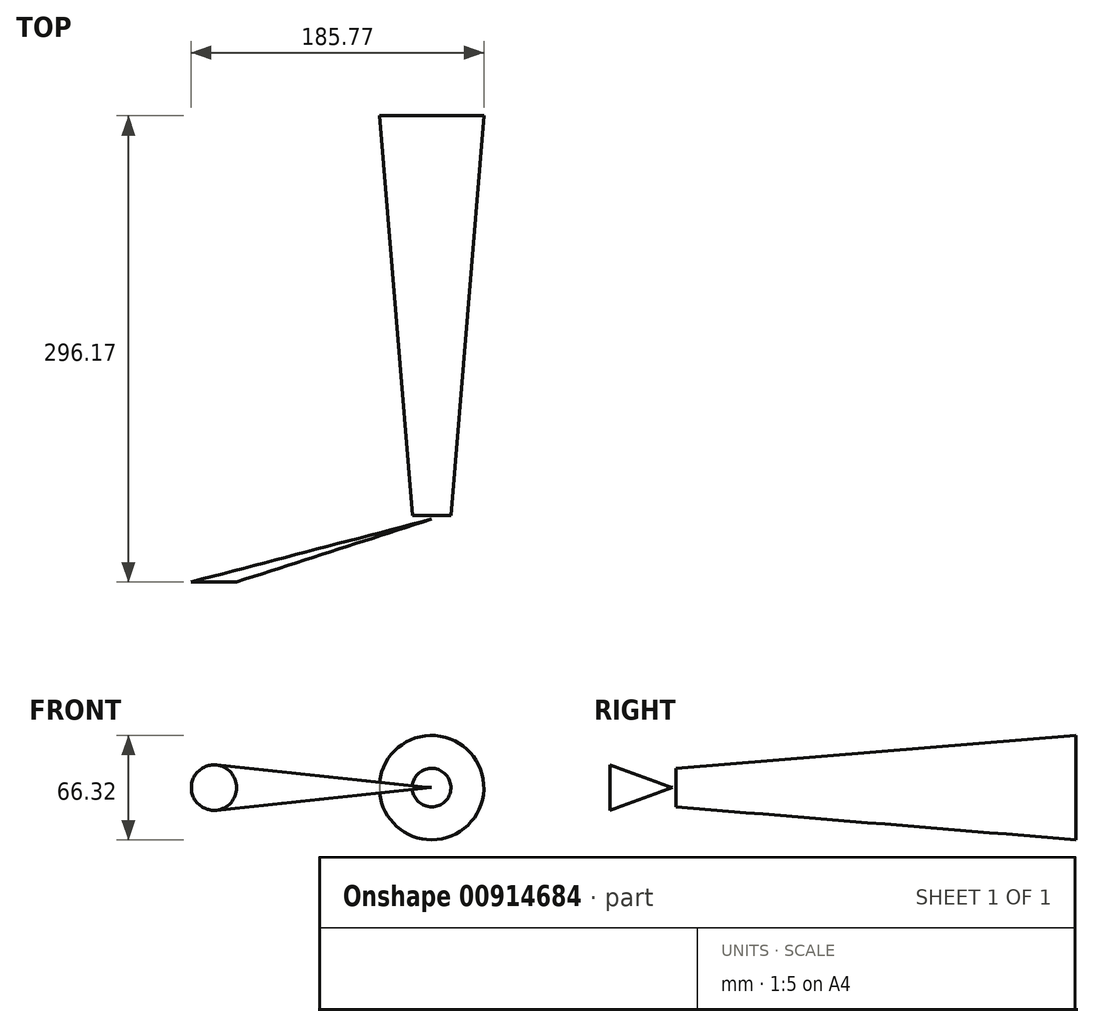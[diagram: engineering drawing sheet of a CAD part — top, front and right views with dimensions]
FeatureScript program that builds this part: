
annotation { "Feature Type Name" : "Feature", "Feature Type Description" : "" }
export const myFeature = defineFeature(function(context is Context, id is Id, definition is map)
    precondition{}
    {
        {
            var Q0;
            Q0=qCreatedBy(makeId("Front.planeOp"),FACE);
            var sketch = newSketch(context, id + "F0", { "sketchPlane" : qUnion([Q0])});
            skCircle(sketch, "E0", {"center": v(0, 0) * mm, "radius": 33.16 * mm});
            skSolve(sketch);
        }
        {
            var Q0;
            Q0=qCreatedBy(makeId("Front.planeOp"),FACE);
            cPlane(context, id + "F1", {"entities" : qUnion([Q0]), "cplaneType" : CPlaneType.OFFSET, "offset" : 254 * mm, "width" : 152.4 * mm, "height" : 152.4 * mm});
        }
        {
            var Q0;
            Q0=qCreatedBy(id+"F1.planeOp",FACE);
            var sketch = newSketch(context, id + "F2", { "sketchPlane" : qUnion([Q0])});
            skCircle(sketch, "E1", {"center": v(0, 0) * mm, "radius": 12.24 * mm});
            skSolve(sketch);
        }
        {
            var Q0;
            Q0=makeQuery(id+"F2.imprint","IMPRINT",FACE,{"disambiguationData":[TD([[makeQuery(id+"F2.imprint","IMPRINT",EDGE,{"derivedFrom":sQuery(id+"F2.wireOp",EDGE,"E1")}),1.0]])]});
            var Q1;
            Q1=makeQuery(id+"F0.imprint","IMPRINT",FACE,{"disambiguationData":[TD([[makeQuery(id+"F0.imprint","IMPRINT",EDGE,{"derivedFrom":sQuery(id+"F0.wireOp",EDGE,"E0")}),1.0]])]});
            loft(context, id + "F3", {"sheetProfilesArray" : [{ "sheetProfileEntities" : qUnion([Q0]) }, { "sheetProfileEntities" : qUnion([Q1]) }]});
        }
        {
            var Q0;
            Q0=qCreatedBy(makeId("Top.planeOp"),FACE);
            var sketch = newSketch(context, id + "F4", { "sketchPlane" : qUnion([Q0])});
            skFitSpline(sketch, "E2", {"points": [v(0, -256.26) * mm, v(-22.34, -348.96) * mm, v(-135.64, -296.17) * mm], "startDerivative": vector(-9.6, -268.25) * mm, "endDerivative": vector(-256.13, 178.36) * mm});
            skSolve(sketch);
        }
        {
            var Q0;
            Q0=sQuery(id+"F4.wireOp",VERTEX,"E2.end");
            var Q1;
            Q1=qCreatedBy(makeId("Front.planeOp"),FACE);
            cPlane(context, id + "F5", {"entities" : qUnion([Q0, Q1]), "cplaneType" : CPlaneType.PLANE_POINT, "offset" : 25.4 * mm, "width" : 152.4 * mm, "height" : 152.4 * mm});
        }
        {
            var Q0;
            Q0=qCreatedBy(id+"F5.planeOp",FACE);
            var sketch = newSketch(context, id + "F6", { "sketchPlane" : qUnion([Q0])});
            skCircle(sketch, "E3", {"center": v(-138.22, 0) * mm, "radius": 14.4 * mm});
            skSolve(sketch);
        }
        {
            var Q0;
            Q0=makeQuery(id+"F6.imprint","IMPRINT",FACE,{"disambiguationData":[TD([[makeQuery(id+"F6.imprint","IMPRINT",EDGE,{"derivedFrom":sQuery(id+"F6.wireOp",EDGE,"E3")}),1.0]])]});
            var Q1;
            Q1=sQuery(id+"F4.wireOp",VERTEX,"E2.start");
            loft(context, id + "F7", {"sheetProfilesArray" : [{ "sheetProfileEntities" : qUnion([Q0]) }, { "sheetProfileEntities" : qUnion([Q1]) }]});
        }
    });
